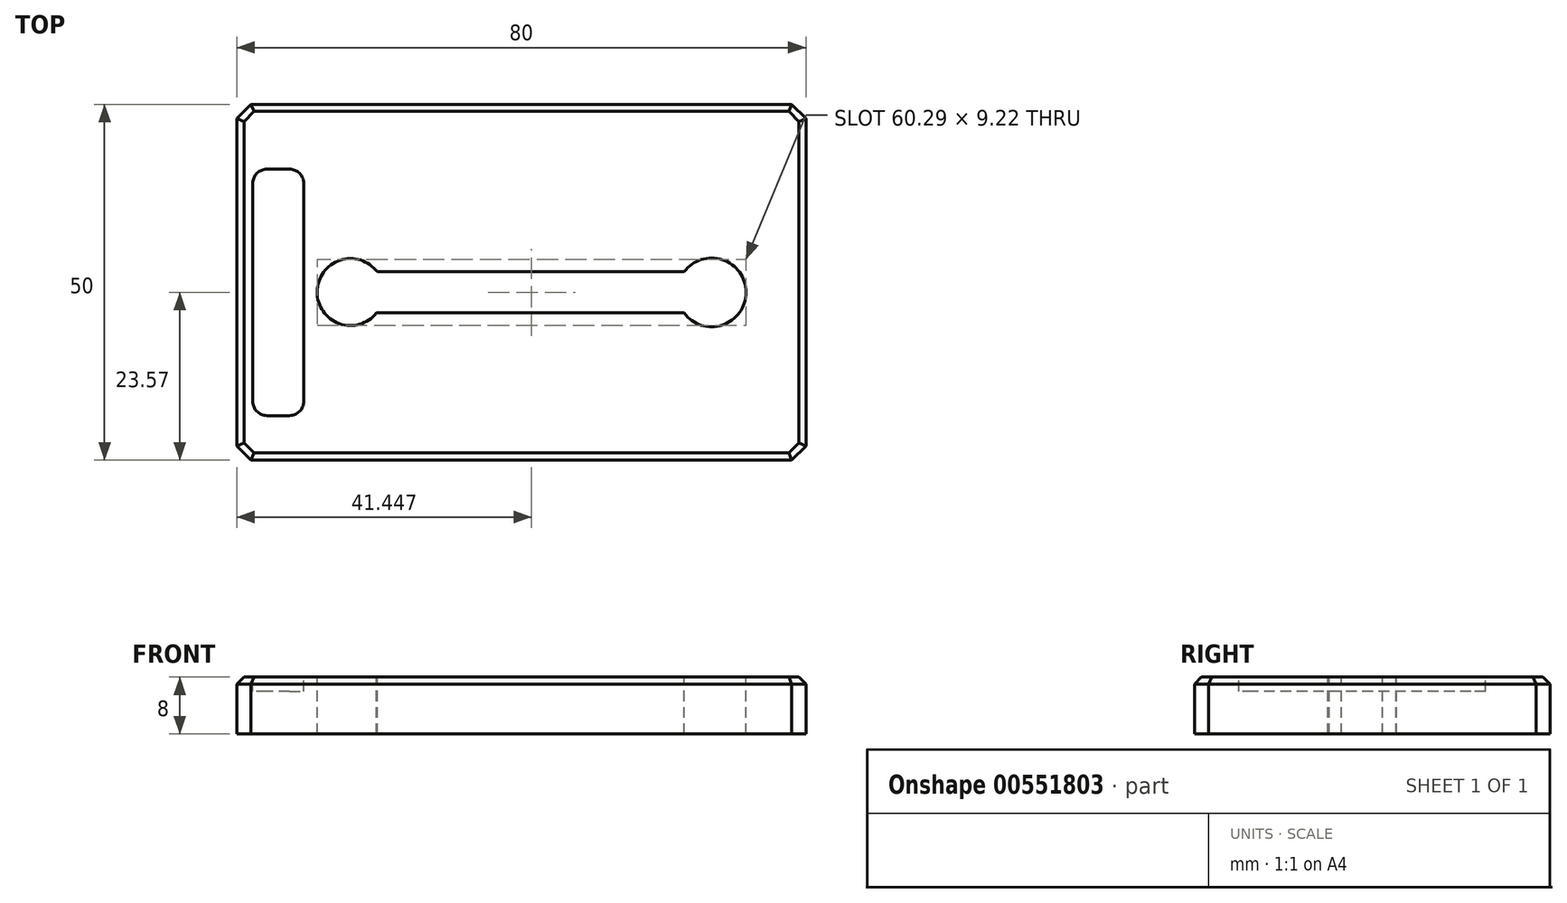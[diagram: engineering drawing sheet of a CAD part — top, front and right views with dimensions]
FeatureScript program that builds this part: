
annotation { "Feature Type Name" : "Feature", "Feature Type Description" : "" }
export const myFeature = defineFeature(function(context is Context, id is Id, definition is map)
    precondition{}
    {
        {
            var Q0;
            Q0=qCreatedBy(makeId("Top.planeOp"),FACE);
            var sketch = newSketch(context, id + "F0", { "sketchPlane" : qUnion([Q0])});
            skLineSegment(sketch, "E0.bottom", {"start": v(-66.76, 26.43) * mm, "end": v(13.24, 26.43) * mm});
            skLineSegment(sketch, "E0.top", {"start": v(-66.76, -23.57) * mm, "end": v(13.24, -23.57) * mm});
            skLineSegment(sketch, "E0.left", {"start": v(-66.76, 26.43) * mm, "end": v(-66.76, -23.57) * mm});
            skLineSegment(sketch, "E0.right", {"start": v(13.24, 26.43) * mm, "end": v(13.24, -23.57) * mm});
            skSolve(sketch);
        }
        {
            var Q0;
            Q0=makeQuery(id+"F0.imprint","IMPRINT",FACE,{"disambiguationData":[TD([[makeQuery(id+"F0.imprint","IMPRINT",EDGE,{"derivedFrom":sQuery(id+"F0.wireOp",EDGE,"E0.bottom")}),-1.0]])]});
            extrude(context, id + "F1", {"entities" : qUnion([Q0]), "depth" : 8 * mm, "offsetDistance" : 25.4 * mm});
        }
        {
            var Q0;
            Q0=makeQuery(id+"F1.opExtrude","CAP_FACE",FACE,{"disambiguationData":[OSD([sQuery(id+"F0.wireOp",EDGE,"E0.bottom"),sQuery(id+"F0.wireOp",EDGE,"E0.top"),sQuery(id+"F0.wireOp",EDGE,"E0.left"),sQuery(id+"F0.wireOp",EDGE,"E0.right")])],"isStart":false});
            var sketch = newSketch(context, id + "F2", { "sketchPlane" : qUnion([Q0])});
            skLineSegment(sketch, "E1.bottom", {"start": v(-3.87, 2.9) * mm, "end": v(-47.02, 2.9) * mm});
            skLineSegment(sketch, "E1.top", {"start": v(-3.87, -2.9) * mm, "end": v(-47.1, -2.9) * mm});
            skPoint(sketch, "E1.middle", {"position": v(-4.7, 0) * mm});
            skArc(sketch, "E2", {"start": v(-47.02, 2.9) * mm, "mid": v(-55.46, 0.1) * mm, "end": v(-47.1, -2.9) * mm});
            skArc(sketch, "E3", {"start": v(-3.87, -2.9) * mm, "mid": v(4.83, 0) * mm, "end": v(-3.87, 2.9) * mm});
            skPoint(sketch, "E4.orphan", {"position": v(-42.64, 2.9) * mm});
            skPoint(sketch, "E5.orphan", {"position": v(-26.43, -2.9) * mm});
            skPoint(sketch, "E6.orphan", {"position": v(33.26, -2.9) * mm});
            skPoint(sketch, "E7.orphan", {"position": v(17.05, 2.9) * mm});
            skSolve(sketch);
        }
        {
            var Q0;
            Q0=makeQuery(id+"F2.imprint","IMPRINT",FACE,{"disambiguationData":[TD([[makeQuery(id+"F2.imprint","IMPRINT",EDGE,{"derivedFrom":sQuery(id+"F2.wireOp",EDGE,"E1.bottom")}),1.0]])]});
            extrude(context, id + "F3", {"entities" : qUnion([Q0]), "operationType" : NewBodyOperationType.REMOVE, "oppositeDirection" : true, "depth" : 25.4 * mm, "offsetDistance" : 25.4 * mm});
        }
        {
            var Q0;
            Q0=makeQuery(id+"F1.opExtrude","CAP_FACE",FACE,{"disambiguationData":[OSD([sQuery(id+"F0.wireOp",EDGE,"E0.bottom"),sQuery(id+"F0.wireOp",EDGE,"E0.top"),sQuery(id+"F0.wireOp",EDGE,"E0.left"),sQuery(id+"F0.wireOp",EDGE,"E0.right")])],"isStart":false});
            var sketch = newSketch(context, id + "F4", { "sketchPlane" : qUnion([Q0])});
            skPoint(sketch, "E8.middle", {"position": v(-60.93, 0) * mm});
            skLineSegment(sketch, "E9.bottom", {"start": v(-59.35, 17.32) * mm, "end": v(-62.5, 17.32) * mm});
            skLineSegment(sketch, "E9.top", {"start": v(-59.35, -17.32) * mm, "end": v(-62.5, -17.32) * mm});
            skLineSegment(sketch, "E9.left", {"start": v(-57.35, 15.32) * mm, "end": v(-57.35, -15.32) * mm});
            skLineSegment(sketch, "E9.right", {"start": v(-64.5, 15.32) * mm, "end": v(-64.5, -15.32) * mm});
            skPoint(sketch, "E10.visualSharp", {"position": v(-57.35, 17.32) * mm});
            skArc(sketch, "E10.filletArc", {"start": v(-57.35, 15.32) * mm, "mid": v(-57.93, 16.73) * mm, "end": v(-59.35, 17.32) * mm});
            skPoint(sketch, "E11.visualSharp", {"position": v(-64.5, 17.32) * mm});
            skArc(sketch, "E11.filletArc", {"start": v(-62.5, 17.32) * mm, "mid": v(-63.92, 16.73) * mm, "end": v(-64.5, 15.32) * mm});
            skPoint(sketch, "E12.visualSharp", {"position": v(-64.5, -17.32) * mm});
            skArc(sketch, "E12.filletArc", {"start": v(-64.5, -15.32) * mm, "mid": v(-63.92, -16.73) * mm, "end": v(-62.5, -17.32) * mm});
            skPoint(sketch, "E13.visualSharp", {"position": v(-57.35, -17.32) * mm});
            skArc(sketch, "E13.filletArc", {"start": v(-59.35, -17.32) * mm, "mid": v(-57.93, -16.73) * mm, "end": v(-57.35, -15.32) * mm});
            skSolve(sketch);
        }
        {
            var Q0;
            Q0=makeQuery(id+"F4.imprint","IMPRINT",FACE,{"disambiguationData":[TD([[makeQuery(id+"F4.imprint","IMPRINT",EDGE,{"derivedFrom":sQuery(id+"F4.wireOp",EDGE,"E9.bottom")}),1.0]])]});
            extrude(context, id + "F5", {"entities" : qUnion([Q0]), "operationType" : NewBodyOperationType.REMOVE, "oppositeDirection" : true, "depth" : 2 * mm, "offsetDistance" : 25.4 * mm});
        }
        {
            var Q0;
            Q0=makeQuery(id+"F1.opExtrude","SWEPT_EDGE",EDGE,{"disambiguationData":[OSD([sQuery(id+"F0.wireOp",EDGE,"E0.bottom"),sQuery(id+"F0.wireOp",EDGE,"E0.right")])]});
            var Q1;
            Q1=makeQuery(id+"F1.opExtrude","SWEPT_EDGE",EDGE,{"disambiguationData":[OSD([sQuery(id+"F0.wireOp",EDGE,"E0.top"),sQuery(id+"F0.wireOp",EDGE,"E0.right")])]});
            var Q2;
            Q2=makeQuery(id+"F1.opExtrude","SWEPT_EDGE",EDGE,{"disambiguationData":[OSD([sQuery(id+"F0.wireOp",EDGE,"E0.top"),sQuery(id+"F0.wireOp",EDGE,"E0.left")])]});
            var Q3;
            Q3=makeQuery(id+"F1.opExtrude","SWEPT_EDGE",EDGE,{"disambiguationData":[OSD([sQuery(id+"F0.wireOp",EDGE,"E0.bottom"),sQuery(id+"F0.wireOp",EDGE,"E0.left")])]});
            chamfer(context, id + "F6", {"entities" : qUnion([Q0, Q1, Q2, Q3]), "width" : 2 * mm, "tangentPropagation" : true});
        }
        {
            var Q0;
            Q0=makeQuery(id+"F1.opExtrude","CAP_EDGE",EDGE,{"disambiguationData":[OSD([sQuery(id+"F0.wireOp",EDGE,"E0.left")])],"isStart":false});
            var Q1;
            Q1=makeQuery(id+"F1.opExtrude","CAP_EDGE",EDGE,{"disambiguationData":[OSD([sQuery(id+"F0.wireOp",EDGE,"E0.bottom")])],"isStart":false});
            var Q2;
            {var subQ0=sQuery(id+"F0.wireOp",EDGE,"E0.left");var subQ1=sQuery(id+"F0.wireOp",EDGE,"E0.bottom");Q2=makeQuery(id+"F6.opChamfer","BLEND_EDGE",EDGE,{"blendedFrom":[makeQuery(id+"F1.opExtrude","SWEPT_EDGE",EDGE,{"disambiguationData":[OSD([subQ1,subQ0])]}),makeQuery(id+"F1.opExtrude","CAP_FACE",FACE,{"disambiguationData":[OSD([subQ1,sQuery(id+"F0.wireOp",EDGE,"E0.top"),subQ0,sQuery(id+"F0.wireOp",EDGE,"E0.right")])],"isStart":false})],"blendedInto":[makeQuery(id+"F1.opExtrude","CAP_FACE",FACE,{"disambiguationData":[OSD([subQ1,sQuery(id+"F0.wireOp",EDGE,"E0.top"),subQ0,sQuery(id+"F0.wireOp",EDGE,"E0.right")])],"isStart":false})]});}
            var Q3;
            {var subQ0=sQuery(id+"F0.wireOp",EDGE,"E0.left");var subQ1=sQuery(id+"F0.wireOp",EDGE,"E0.top");Q3=makeQuery(id+"F6.opChamfer","BLEND_EDGE",EDGE,{"blendedFrom":[makeQuery(id+"F1.opExtrude","SWEPT_EDGE",EDGE,{"disambiguationData":[OSD([subQ1,subQ0])]}),makeQuery(id+"F1.opExtrude","CAP_FACE",FACE,{"disambiguationData":[OSD([sQuery(id+"F0.wireOp",EDGE,"E0.bottom"),subQ1,subQ0,sQuery(id+"F0.wireOp",EDGE,"E0.right")])],"isStart":false})],"blendedInto":[makeQuery(id+"F1.opExtrude","CAP_FACE",FACE,{"disambiguationData":[OSD([sQuery(id+"F0.wireOp",EDGE,"E0.bottom"),subQ1,subQ0,sQuery(id+"F0.wireOp",EDGE,"E0.right")])],"isStart":false})]});}
            var Q4;
            Q4=makeQuery(id+"F1.opExtrude","CAP_EDGE",EDGE,{"disambiguationData":[OSD([sQuery(id+"F0.wireOp",EDGE,"E0.right")])],"isStart":false});
            var Q5;
            {var subQ0=sQuery(id+"F0.wireOp",EDGE,"E0.right");var subQ1=sQuery(id+"F0.wireOp",EDGE,"E0.bottom");Q5=makeQuery(id+"F6.opChamfer","BLEND_EDGE",EDGE,{"blendedFrom":[makeQuery(id+"F1.opExtrude","SWEPT_EDGE",EDGE,{"disambiguationData":[OSD([subQ1,subQ0])]}),makeQuery(id+"F1.opExtrude","CAP_FACE",FACE,{"disambiguationData":[OSD([subQ1,sQuery(id+"F0.wireOp",EDGE,"E0.top"),sQuery(id+"F0.wireOp",EDGE,"E0.left"),subQ0])],"isStart":false})],"blendedInto":[makeQuery(id+"F1.opExtrude","CAP_FACE",FACE,{"disambiguationData":[OSD([subQ1,sQuery(id+"F0.wireOp",EDGE,"E0.top"),sQuery(id+"F0.wireOp",EDGE,"E0.left"),subQ0])],"isStart":false})]});}
            var Q6;
            {var subQ0=sQuery(id+"F0.wireOp",EDGE,"E0.right");var subQ1=sQuery(id+"F0.wireOp",EDGE,"E0.top");Q6=makeQuery(id+"F6.opChamfer","BLEND_EDGE",EDGE,{"blendedFrom":[makeQuery(id+"F1.opExtrude","SWEPT_EDGE",EDGE,{"disambiguationData":[OSD([subQ1,subQ0])]}),makeQuery(id+"F1.opExtrude","CAP_FACE",FACE,{"disambiguationData":[OSD([sQuery(id+"F0.wireOp",EDGE,"E0.bottom"),subQ1,sQuery(id+"F0.wireOp",EDGE,"E0.left"),subQ0])],"isStart":false})],"blendedInto":[makeQuery(id+"F1.opExtrude","CAP_FACE",FACE,{"disambiguationData":[OSD([sQuery(id+"F0.wireOp",EDGE,"E0.bottom"),subQ1,sQuery(id+"F0.wireOp",EDGE,"E0.left"),subQ0])],"isStart":false})]});}
            var Q7;
            Q7=makeQuery(id+"F1.opExtrude","CAP_EDGE",EDGE,{"disambiguationData":[OSD([sQuery(id+"F0.wireOp",EDGE,"E0.top")])],"isStart":false});
            chamfer(context, id + "F7", {"entities" : qUnion([Q0, Q1, Q2, Q3, Q4, Q5, Q6, Q7]), "width" : 1 * mm, "tangentPropagation" : true});
        }
    });
